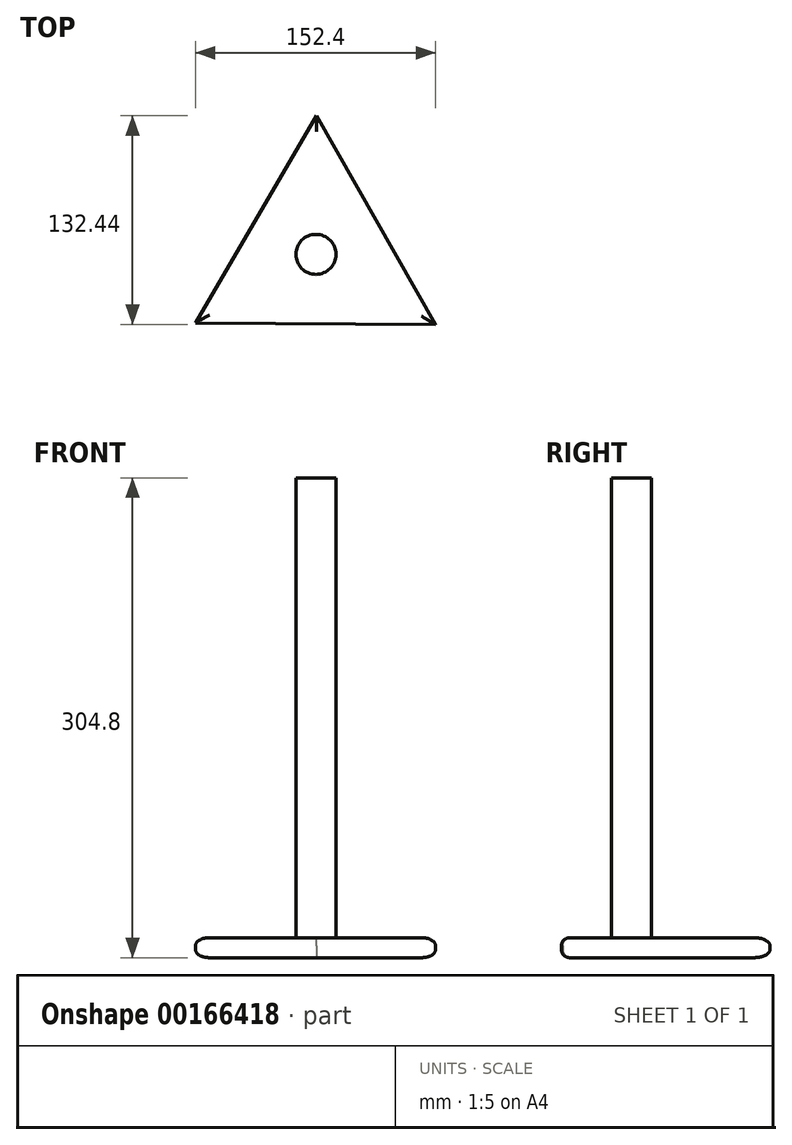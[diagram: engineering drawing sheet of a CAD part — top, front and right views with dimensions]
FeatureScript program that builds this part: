
annotation { "Feature Type Name" : "Feature", "Feature Type Description" : "" }
export const myFeature = defineFeature(function(context is Context, id is Id, definition is map)
    precondition{}
    {
        {
            var Q0;
            Q0=qCreatedBy(makeId("Top.planeOp"),FACE);
            var sketch = newSketch(context, id + "F0", { "sketchPlane" : qUnion([Q0])});
            skCircle(sketch, "E0.cCircle", {"center": v(0, 0) * mm, "radius": 44 * mm, "construction": true});
            skLineSegment(sketch, "E0.0", {"start": v(-76.46, -43.54) * mm, "end": v(0.53, 87.99) * mm});
            skLineSegment(sketch, "E0.1", {"start": v(0.53, 87.99) * mm, "end": v(75.94, -44.45) * mm});
            skLineSegment(sketch, "E0.2", {"start": v(75.94, -44.45) * mm, "end": v(-76.46, -43.54) * mm});
            skPoint(sketch, "E0.0.midPoint", {"position": v(-37.97, 22.22) * mm});
            skSolve(sketch);
        }
        {
            var Q0;
            Q0=makeQuery(id+"F0.imprint","IMPRINT",FACE,{"disambiguationData":[TD([[makeQuery(id+"F0.imprint","IMPRINT",EDGE,{"derivedFrom":sQuery(id+"F0.wireOp",EDGE,"E0.0")}),-1.0]])]});
            extrude(context, id + "F1", {"entities" : qUnion([Q0]), "depth" : 12.7 * mm});
        }
        {
            var Q0;
            Q0=qCreatedBy(makeId("Top.planeOp"),FACE);
            var sketch = newSketch(context, id + "F2", { "sketchPlane" : qUnion([Q0])});
            skCircle(sketch, "E1", {"center": v(0, 0) * mm, "radius": 12.7 * mm});
            skSolve(sketch);
        }
        {
            var Q0;
            Q0 = qSketchRegion(id + "F2", true);
            extrude(context, id + "F3", {"entities" : qUnion([Q0]), "operationType" : NewBodyOperationType.ADD, "depth" : 304.8 * mm});
        }
        {
            var Q0;
            Q0=makeQuery(id+"F1.opExtrude","CAP_EDGE",EDGE,{"disambiguationData":[OSD([sQuery(id+"F0.wireOp",EDGE,"E0.0")])],"isStart":false});
            var Q1;
            Q1=makeQuery(id+"F1.opExtrude","CAP_EDGE",EDGE,{"disambiguationData":[OSD([sQuery(id+"F0.wireOp",EDGE,"E0.1")])],"isStart":false});
            var Q2;
            Q2=makeQuery(id+"F1.opExtrude","CAP_EDGE",EDGE,{"disambiguationData":[OSD([sQuery(id+"F0.wireOp",EDGE,"E0.2")])],"isStart":false});
            fillet(context, id + "F4", {"entities" : qUnion([Q0, Q1, Q2]), "radius" : 5.08 * mm, "tangentPropagation" : true, "allowEdgeOverflow" : false});
        }
        {
            var Q0;
            Q0=makeQuery(id+"F1.opExtrude","CAP_EDGE",EDGE,{"disambiguationData":[OSD([sQuery(id+"F0.wireOp",EDGE,"E0.1")])],"isStart":true});
            var Q1;
            Q1=makeQuery(id+"F1.opExtrude","CAP_EDGE",EDGE,{"disambiguationData":[OSD([sQuery(id+"F0.wireOp",EDGE,"E0.0")])],"isStart":true});
            var Q2;
            Q2=makeQuery(id+"F1.opExtrude","CAP_EDGE",EDGE,{"disambiguationData":[OSD([sQuery(id+"F0.wireOp",EDGE,"E0.2")])],"isStart":true});
            fillet(context, id + "F5", {"entities" : qUnion([Q0, Q1, Q2]), "radius" : 5.08 * mm, "tangentPropagation" : true, "allowEdgeOverflow" : false});
        }
    });
